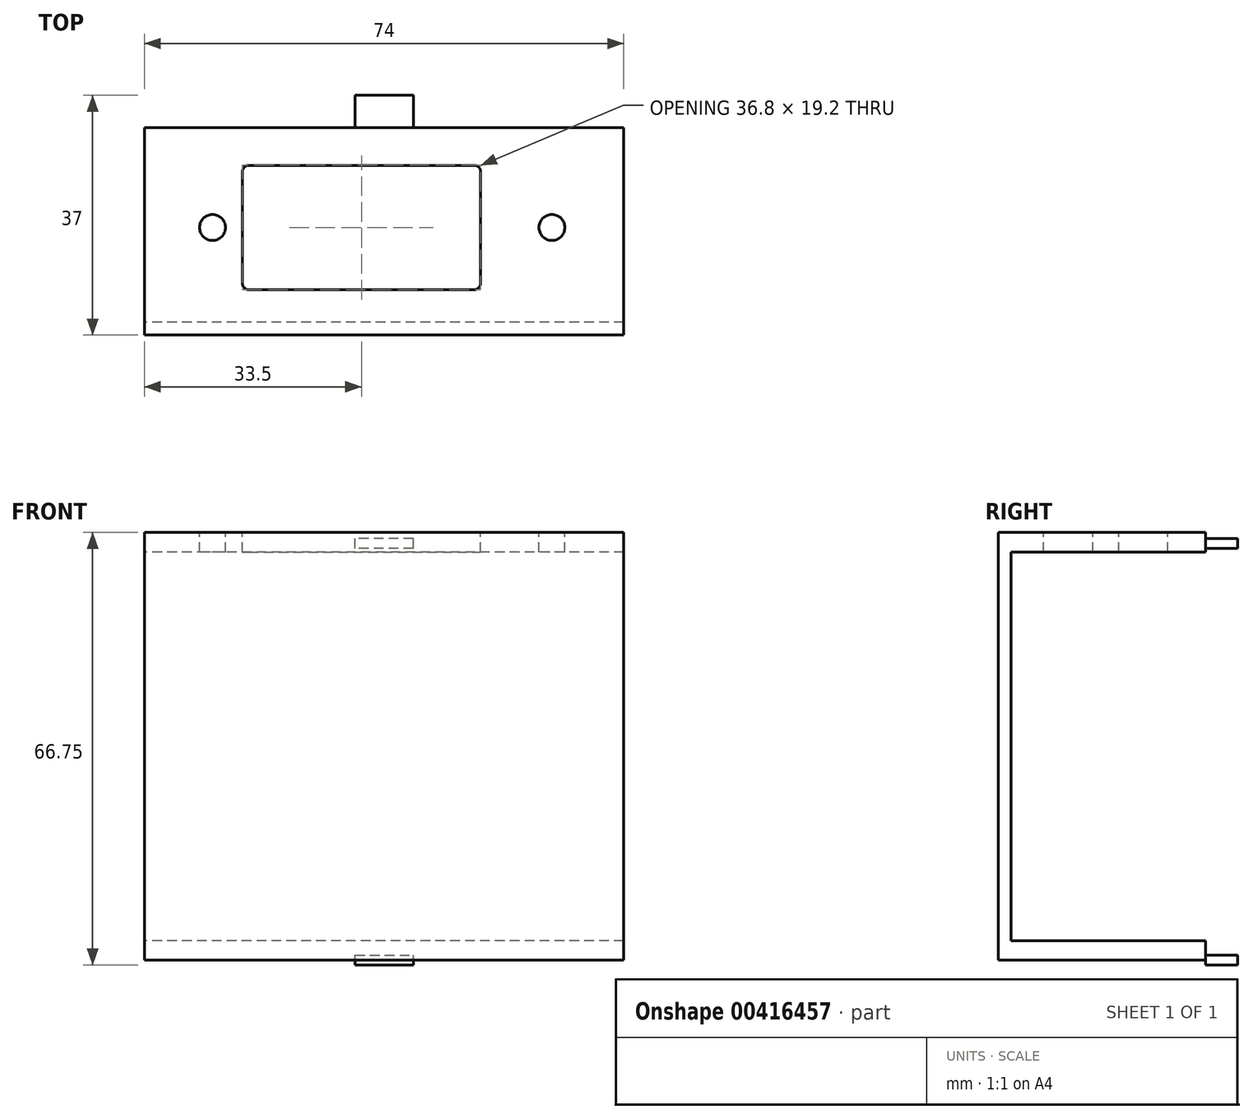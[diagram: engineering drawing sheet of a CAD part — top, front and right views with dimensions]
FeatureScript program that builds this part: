
annotation { "Feature Type Name" : "Feature", "Feature Type Description" : "" }
export const myFeature = defineFeature(function(context is Context, id is Id, definition is map)
    precondition{}
    {
        {
            var Q0;
            Q0=qCreatedBy(makeId("Top.planeOp"),FACE);
            var sketch = newSketch(context, id + "F0", { "sketchPlane" : qUnion([Q0])});
            skLineSegment(sketch, "E0.bottom", {"start": v(37, 16) * mm, "end": v(-37, 16) * mm});
            skLineSegment(sketch, "E0.top", {"start": v(37, -16) * mm, "end": v(-37, -16) * mm});
            skLineSegment(sketch, "E0.left", {"start": v(37, 16) * mm, "end": v(37, -16) * mm});
            skLineSegment(sketch, "E0.right", {"start": v(-37, 16) * mm, "end": v(-37, -16) * mm});
            skPoint(sketch, "E0.middle", {"position": v(0, 0) * mm});
            skSolve(sketch);
        }
        {
            var Q0;
            Q0=makeQuery(id+"F0.imprint","IMPRINT",FACE,{"disambiguationData":[TD([[makeQuery(id+"F0.imprint","IMPRINT",EDGE,{"derivedFrom":sQuery(id+"F0.wireOp",EDGE,"E0.bottom")}),1.0]])]});
            extrude(context, id + "F1", {"entities" : qUnion([Q0]), "depth" : 3 * mm});
        }
        {
            var Q0;
            Q0=makeQuery(id+"F1.opExtrude","CAP_FACE",FACE,{"disambiguationData":[OSD([sQuery(id+"F0.wireOp",EDGE,"E0.bottom"),sQuery(id+"F0.wireOp",EDGE,"E0.top"),sQuery(id+"F0.wireOp",EDGE,"E0.left"),sQuery(id+"F0.wireOp",EDGE,"E0.right")])],"isStart":false});
            var sketch = newSketch(context, id + "F2", { "sketchPlane" : qUnion([Q0])});
            skLineSegment(sketch, "E1.bottom", {"start": v(14.9, -9) * mm, "end": v(-21.9, -9) * mm});
            skLineSegment(sketch, "E1.top", {"start": v(14.9, 10.2) * mm, "end": v(-21.9, 10.2) * mm});
            skLineSegment(sketch, "E1.left", {"start": v(14.9, -9) * mm, "end": v(14.9, 10.2) * mm});
            skLineSegment(sketch, "E1.right", {"start": v(-21.9, -9) * mm, "end": v(-21.9, 10.2) * mm});
            skPoint(sketch, "E1.middle", {"position": v(-3.5, 0) * mm});
            skSolve(sketch);
        }
        {
            var Q0;
            Q0 = qSketchRegion(id + "F2", true);
            var Q1;
            Q1=makeQuery(id+"F1.opExtrude","CAP_FACE",FACE,{"disambiguationData":[OSD([sQuery(id+"F0.wireOp",EDGE,"E0.bottom"),sQuery(id+"F0.wireOp",EDGE,"E0.top"),sQuery(id+"F0.wireOp",EDGE,"E0.left"),sQuery(id+"F0.wireOp",EDGE,"E0.right")])],"isStart":true});
            extrude(context, id + "F3", {"entities" : qUnion([Q0]), "operationType" : NewBodyOperationType.REMOVE, "endBound" : BoundingType.UP_TO_SURFACE, "oppositeDirection" : true, "endBoundEntityFace" : qUnion([Q1]), "depth" : 25 * mm});
        }
        {
            var Q0;
            Q0=makeQuery(id+"F3.boolean.opBoolean","COPY",EDGE,{"derivedFrom":makeQuery(id+"F3.opExtrude","SWEPT_EDGE",EDGE,{"disambiguationData":[OSD([sQuery(id+"F2.wireOp",EDGE,"E1.top"),sQuery(id+"F2.wireOp",EDGE,"E1.right")])]})});
            var Q1;
            Q1=makeQuery(id+"F3.boolean.opBoolean","COPY",EDGE,{"derivedFrom":makeQuery(id+"F3.opExtrude","SWEPT_EDGE",EDGE,{"disambiguationData":[OSD([sQuery(id+"F2.wireOp",EDGE,"E1.bottom"),sQuery(id+"F2.wireOp",EDGE,"E1.right")])]})});
            var Q2;
            Q2=makeQuery(id+"F3.boolean.opBoolean","COPY",EDGE,{"derivedFrom":makeQuery(id+"F3.opExtrude","SWEPT_EDGE",EDGE,{"disambiguationData":[OSD([sQuery(id+"F2.wireOp",EDGE,"E1.top"),sQuery(id+"F2.wireOp",EDGE,"E1.left")])]})});
            var Q3;
            Q3=makeQuery(id+"F3.boolean.opBoolean","COPY",EDGE,{"derivedFrom":makeQuery(id+"F3.opExtrude","SWEPT_EDGE",EDGE,{"disambiguationData":[OSD([sQuery(id+"F2.wireOp",EDGE,"E1.bottom"),sQuery(id+"F2.wireOp",EDGE,"E1.left")])]})});
            fillet(context, id + "F4", {"entities" : qUnion([Q0, Q1, Q2, Q3]), "radius" : 1 * mm, "tangentPropagation" : true, "allowEdgeOverflow" : false});
        }
        {
            var Q0;
            Q0=makeQuery(id+"F1.opExtrude","CAP_FACE",FACE,{"disambiguationData":[OSD([sQuery(id+"F0.wireOp",EDGE,"E0.bottom"),sQuery(id+"F0.wireOp",EDGE,"E0.top"),sQuery(id+"F0.wireOp",EDGE,"E0.left"),sQuery(id+"F0.wireOp",EDGE,"E0.right")])],"isStart":false});
            var sketch = newSketch(context, id + "F5", { "sketchPlane" : qUnion([Q0])});
            skLineSegment(sketch, "E2", {"start": v(-47.1, 0.6) * mm, "end": v(42.57, 0.6) * mm, "construction": true});
            skCircle(sketch, "E3", {"center": v(-26.5, 0.6) * mm, "radius": 2 * mm});
            skCircle(sketch, "E4", {"center": v(25.9, 0.6) * mm, "radius": 2 * mm});
            skSolve(sketch);
        }
        {
            var Q0;
            Q0 = qSketchRegion(id + "F5", true);
            extrude(context, id + "F6", {"entities" : qUnion([Q0]), "operationType" : NewBodyOperationType.REMOVE, "oppositeDirection" : true, "depth" : 25 * mm});
        }
        {
            var Q0;
            Q0=makeQuery(id+"F1.opExtrude","SWEPT_FACE",FACE,{"disambiguationData":[OSD([sQuery(id+"F0.wireOp",EDGE,"E0.bottom")])]});
            var sketch = newSketch(context, id + "F7", { "sketchPlane" : qUnion([Q0])});
            skLineSegment(sketch, "E5.bottom", {"start": v(-4.5, 0.56) * mm, "end": v(4.5, 0.56) * mm});
            skLineSegment(sketch, "E5.top", {"start": v(-4.5, 2.06) * mm, "end": v(4.5, 2.06) * mm});
            skLineSegment(sketch, "E5.left", {"start": v(-4.5, 0.56) * mm, "end": v(-4.5, 2.06) * mm});
            skLineSegment(sketch, "E5.right", {"start": v(4.5, 0.56) * mm, "end": v(4.5, 2.06) * mm});
            skPoint(sketch, "E5.middle", {"position": v(0, 1.3) * mm});
            skPoint(sketch, "E5.middle.positionSnap0", {"position": v(0, 3) * mm});
            skPoint(sketch, "E5.centerSnap0", {"position": v(0, 3) * mm});
            skSolve(sketch);
        }
        {
            var Q0;
            Q0 = qSketchRegion(id + "F7", true);
            extrude(context, id + "F8", {"entities" : qUnion([Q0]), "operationType" : NewBodyOperationType.ADD, "depth" : 5 * mm});
        }
        {
            var Q0;
            Q0=makeQuery(id+"F1.opExtrude","CAP_FACE",FACE,{"disambiguationData":[OSD([sQuery(id+"F0.wireOp",EDGE,"E0.bottom"),sQuery(id+"F0.wireOp",EDGE,"E0.top"),sQuery(id+"F0.wireOp",EDGE,"E0.left"),sQuery(id+"F0.wireOp",EDGE,"E0.right")])],"isStart":true});
            var sketch = newSketch(context, id + "F9", { "sketchPlane" : qUnion([Q0])});
            skLineSegment(sketch, "E6.bottom", {"start": v(37, 16) * mm, "end": v(-37, 16) * mm});
            skLineSegment(sketch, "E6.top", {"start": v(37, 14) * mm, "end": v(-37, 14) * mm});
            skLineSegment(sketch, "E6.left", {"start": v(37, 16) * mm, "end": v(37, 14) * mm});
            skLineSegment(sketch, "E6.right", {"start": v(-37, 16) * mm, "end": v(-37, 14) * mm});
            skSolve(sketch);
        }
        {
            var Q0;
            Q0 = qSketchRegion(id + "F9", true);
            extrude(context, id + "F10", {"entities" : qUnion([Q0]), "operationType" : NewBodyOperationType.ADD, "depth" : 60 * mm});
        }
        {
            var Q0;
            Q0=makeQuery(id+"F10.opExtrude","CAP_FACE",FACE,{"disambiguationData":[OSD([sQuery(id+"F9.wireOp",EDGE,"E6.bottom"),sQuery(id+"F9.wireOp",EDGE,"E6.top"),sQuery(id+"F9.wireOp",EDGE,"E6.left"),sQuery(id+"F9.wireOp",EDGE,"E6.right")])],"isStart":false});
            var sketch = newSketch(context, id + "F11", { "sketchPlane" : qUnion([Q0])});
            skLineSegment(sketch, "E7.bottom", {"start": v(37, 16) * mm, "end": v(-37, 16) * mm});
            skLineSegment(sketch, "E7.top", {"start": v(37, -16) * mm, "end": v(-37, -16) * mm});
            skLineSegment(sketch, "E7.left", {"start": v(37, 16) * mm, "end": v(37, -16) * mm});
            skLineSegment(sketch, "E7.right", {"start": v(-37, 16) * mm, "end": v(-37, -16) * mm});
            skSolve(sketch);
        }
        {
            var Q0;
            Q0 = qSketchRegion(id + "F11", true);
            extrude(context, id + "F12", {"entities" : qUnion([Q0]), "operationType" : NewBodyOperationType.ADD, "depth" : 3 * mm});
        }
        {
            var Q0;
            Q0=makeQuery(id+"F12.opExtrude","SWEPT_FACE",FACE,{"disambiguationData":[OSD([sQuery(id+"F11.wireOp",EDGE,"E7.top")])]});
            var sketch = newSketch(context, id + "F13", { "sketchPlane" : qUnion([Q0])});
            skLineSegment(sketch, "E8.bottom", {"start": v(4.5, -63.75) * mm, "end": v(-4.5, -63.75) * mm});
            skLineSegment(sketch, "E8.top", {"start": v(4.5, -62.25) * mm, "end": v(-4.5, -62.25) * mm});
            skLineSegment(sketch, "E8.left", {"start": v(4.5, -63.75) * mm, "end": v(4.5, -62.25) * mm});
            skLineSegment(sketch, "E8.right", {"start": v(-4.5, -63.75) * mm, "end": v(-4.5, -62.25) * mm});
            skPoint(sketch, "E8.middle", {"position": v(0, -63) * mm});
            skSolve(sketch);
        }
        {
            var Q0;
            Q0 = qSketchRegion(id + "F13", true);
            extrude(context, id + "F14", {"entities" : qUnion([Q0]), "operationType" : NewBodyOperationType.ADD, "depth" : 5 * mm});
        }
    });
